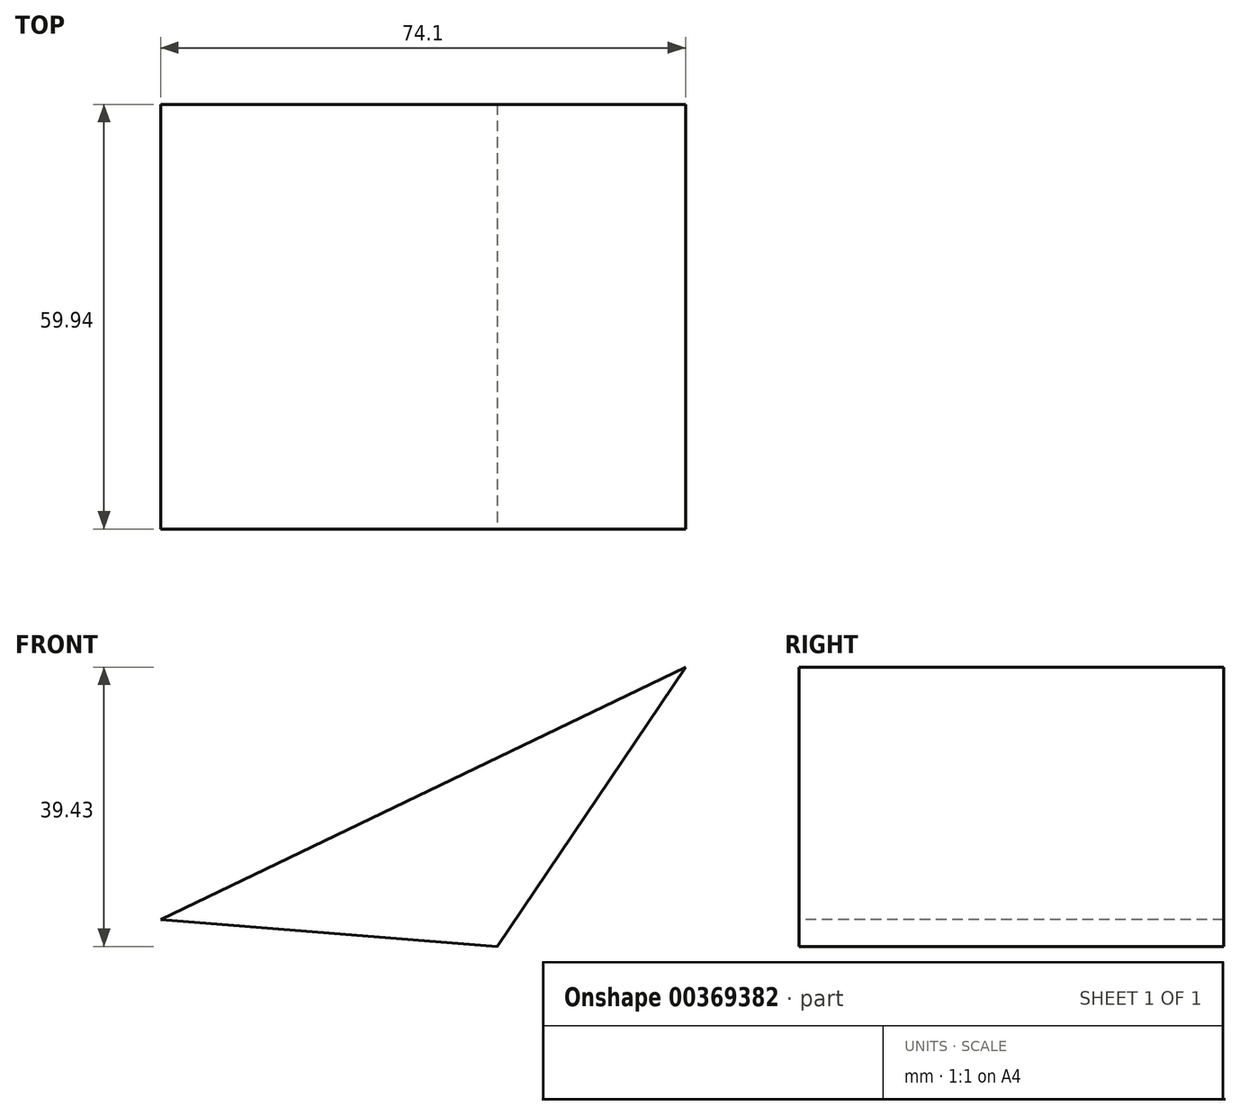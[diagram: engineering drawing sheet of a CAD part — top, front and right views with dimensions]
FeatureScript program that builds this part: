
annotation { "Feature Type Name" : "Feature", "Feature Type Description" : "" }
export const myFeature = defineFeature(function(context is Context, id is Id, definition is map)
    precondition{}
    {
        {
            var Q0;
            Q0=qCreatedBy(makeId("Front.planeOp"),FACE);
            var sketch = newSketch(context, id + "F0", { "sketchPlane" : qUnion([Q0])});
            skLineSegment(sketch, "E0", {"start": v(-66.23, 15.4) * mm, "end": v(7.87, 51.03) * mm});
            skLineSegment(sketch, "E1", {"start": v(7.87, 51.03) * mm, "end": v(-18.73, 11.6) * mm});
            skLineSegment(sketch, "E2", {"start": v(-18.73, 11.6) * mm, "end": v(-66.23, 15.4) * mm});
            skSolve(sketch);
        }
        {
            var Q0;
            Q0 = qSketchRegion(id + "F0", true);
            extrude(context, id + "F1", {"entities" : qUnion([Q0]), "oppositeDirection" : true, "depth" : 59.94 * mm});
        }
    });
